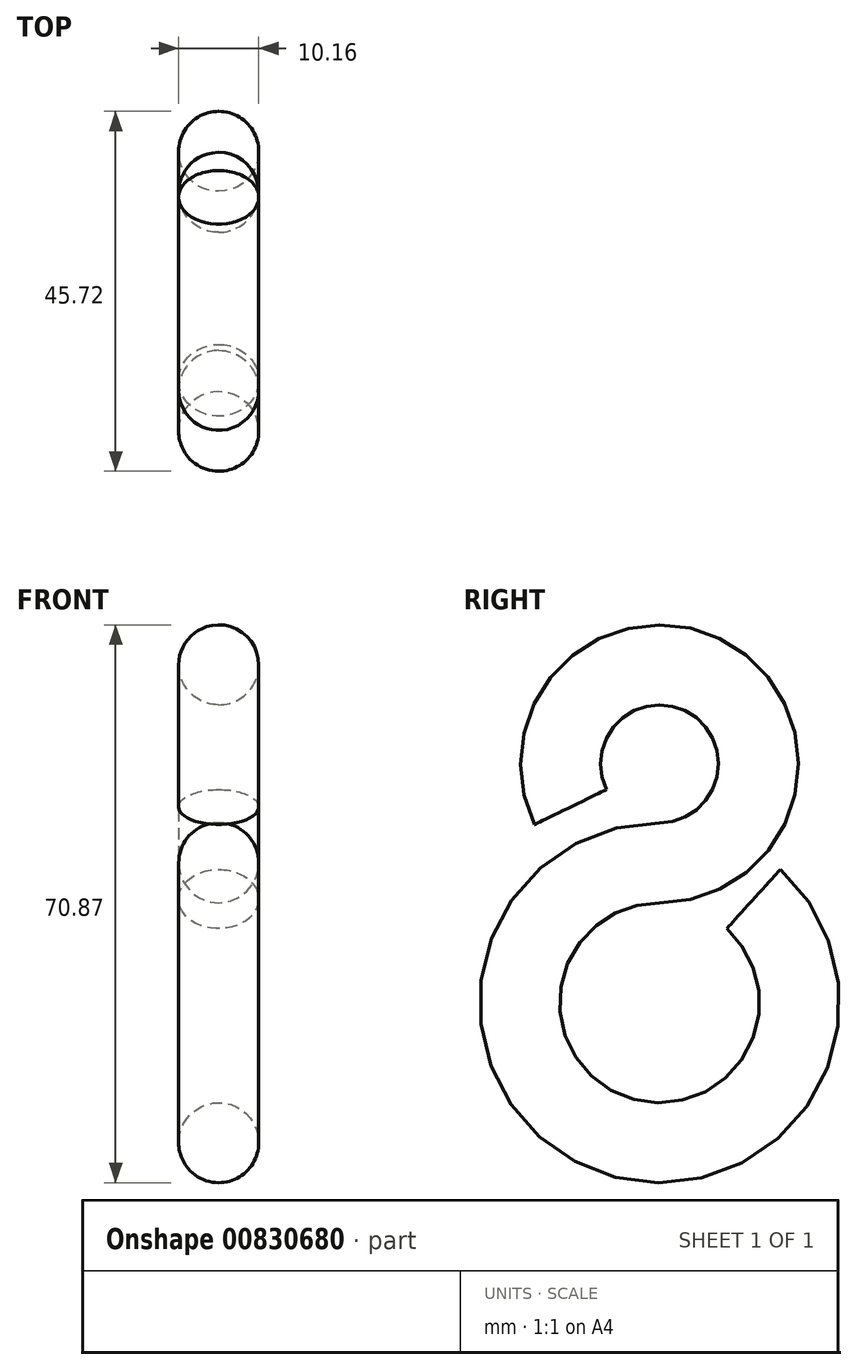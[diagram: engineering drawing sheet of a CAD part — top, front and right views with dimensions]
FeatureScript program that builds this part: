
annotation { "Feature Type Name" : "Feature", "Feature Type Description" : "" }
export const myFeature = defineFeature(function(context is Context, id is Id, definition is map)
    precondition{}
    {
        {
            var Q0;
            Q0=qCreatedBy(makeId("Right.planeOp"),FACE);
            var sketch = newSketch(context, id + "F0", { "sketchPlane" : qUnion([Q0])});
            skPoint(sketch, "E0", {"position": v(0, 12.57) * mm});
            skArc(sketch, "E1", {"start": v(0, 0) * mm, "mid": v(6.67, 23.23) * mm, "end": v(-11.3, 7.08) * mm});
            skPoint(sketch, "E2", {"position": v(0, -17.78) * mm});
            skArc(sketch, "E3", {"start": v(0, 0) * mm, "mid": v(-6.4, -34.37) * mm, "end": v(11.95, -4.61) * mm});
            skSolve(sketch);
        }
        {
            var Q0;
            Q0=sQuery(id+"F0.wireOp",VERTEX,"E1.end");
            var Q1;
            Q1=sQuery(id+"F0.wireOp",EDGE,"E1");
            cPlane(context, id + "F1", {"entities" : qUnion([Q0, Q1]), "cplaneType" : CPlaneType.CURVE_POINT, "offset" : 25.4 * mm, "width" : 152.4 * mm, "height" : 152.4 * mm});
        }
        {
            var Q0;
            Q0=qCreatedBy(id+"F1.planeOp",FACE);
            var sketch = newSketch(context, id + "F2", { "sketchPlane" : qUnion([Q0])});
            skPoint(sketch, "E4", {"position": v(0, 7.08) * mm});
            skCircle(sketch, "E5", {"center": v(0, 7.08) * mm, "radius": 5.08 * mm});
            skSolve(sketch);
        }
        {
            var Q0;
            Q0=makeQuery(id+"F2.imprint","IMPRINT",FACE,{"disambiguationData":[TD([[makeQuery(id+"F2.imprint","IMPRINT",EDGE,{"derivedFrom":sQuery(id+"F2.wireOp",EDGE,"E5")}),1.0]])]});
            var Q1;
            Q1=sQuery(id+"F0.wireOp",EDGE,"E1");
            var Q2;
            Q2=sQuery(id+"F0.wireOp",EDGE,"zpw7CeA8-yreD-1TFA-5RaI-wsoIKEkLq81x");
            var Q3;
            Q3=sQuery(id+"F0.wireOp",EDGE,"E3");
            sweep(context, id + "F3", {"profiles" : qUnion([Q0]), "path" : qUnion([Q1, Q2, Q3])});
        }
    });
